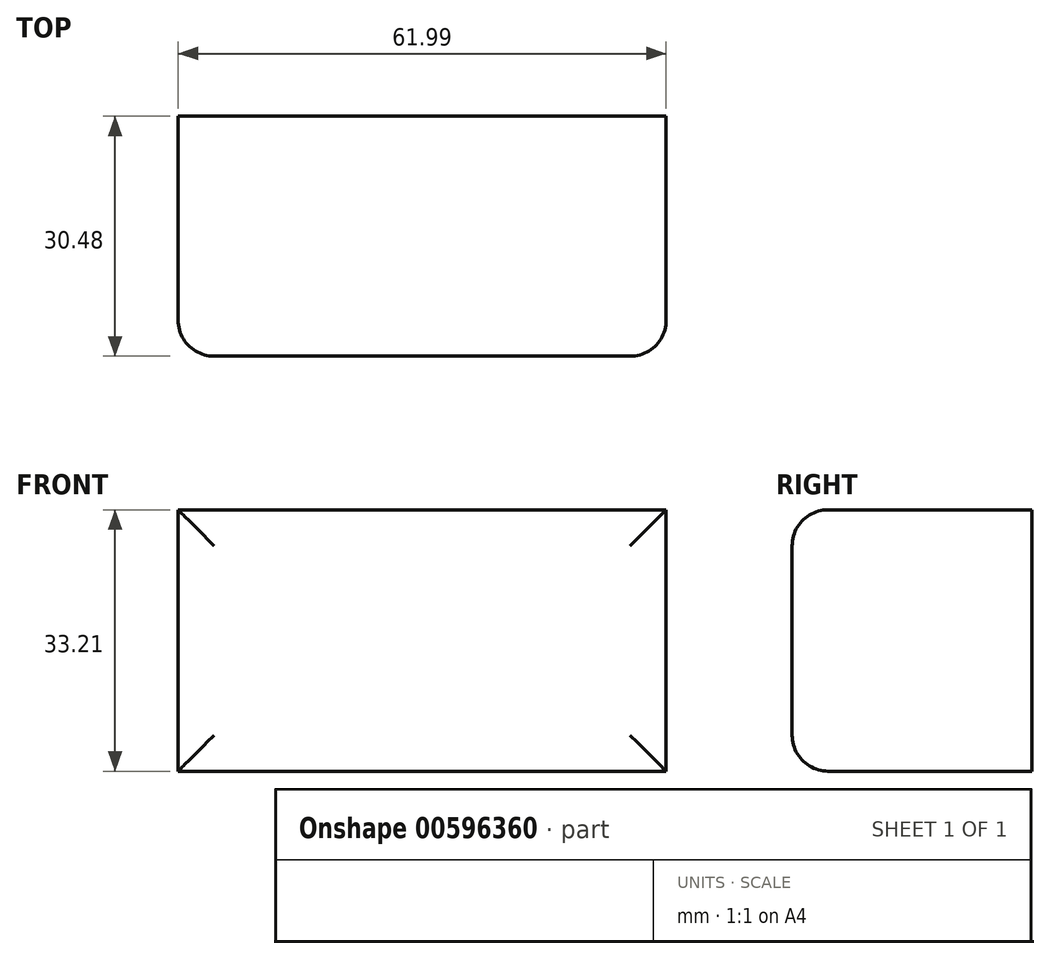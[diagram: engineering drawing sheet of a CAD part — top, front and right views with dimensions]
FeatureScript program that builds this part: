
annotation { "Feature Type Name" : "Feature", "Feature Type Description" : "" }
export const myFeature = defineFeature(function(context is Context, id is Id, definition is map)
    precondition{}
    {
        {
            var Q0;
            Q0=qCreatedBy(makeId("Front.planeOp"),FACE);
            var sketch = newSketch(context, id + "F0", { "sketchPlane" : qUnion([Q0])});
            skLineSegment(sketch, "E0.bottom", {"start": v(-72.71, 74.8) * mm, "end": v(-10.72, 74.8) * mm});
            skLineSegment(sketch, "E0.top", {"start": v(-72.71, 41.59) * mm, "end": v(-10.72, 41.59) * mm});
            skLineSegment(sketch, "E0.left", {"start": v(-72.71, 74.8) * mm, "end": v(-72.71, 41.59) * mm});
            skLineSegment(sketch, "E0.right", {"start": v(-10.72, 74.8) * mm, "end": v(-10.72, 41.59) * mm});
            skSolve(sketch);
        }
        {
            var Q0;
            Q0 = qSketchRegion(id + "F0", true);
            extrude(context, id + "F1", {"entities" : qUnion([Q0]), "depth" : 30.48 * mm, "offsetDistance" : 30.48 * mm});
        }
        {
            var Q0;
            Q0=makeQuery(id+"F1.opExtrude","CAP_FACE",FACE,{"disambiguationData":[OSD([sQuery(id+"F0.wireOp",EDGE,"E0.bottom"),sQuery(id+"F0.wireOp",EDGE,"E0.top"),sQuery(id+"F0.wireOp",EDGE,"E0.left"),sQuery(id+"F0.wireOp",EDGE,"E0.right")])],"isStart":false});
            fillet(context, id + "F2", {"entities" : qUnion([Q0]), "radius" : 4.57 * mm, "tangentPropagation" : true, "allowEdgeOverflow" : false});
        }
    });
